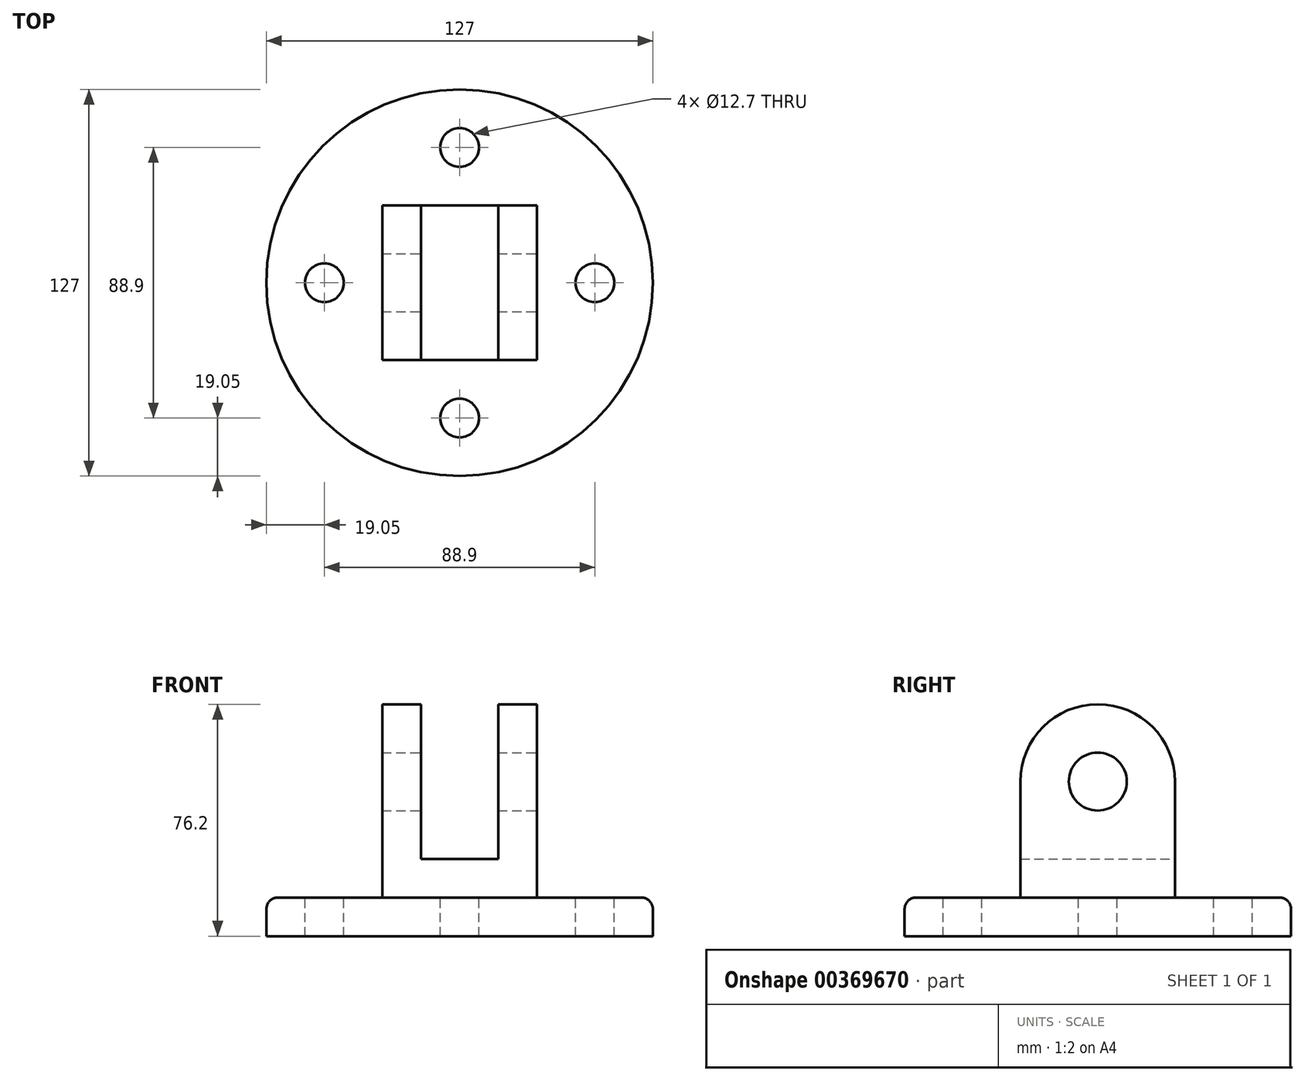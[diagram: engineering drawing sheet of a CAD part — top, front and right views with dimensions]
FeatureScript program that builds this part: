
annotation { "Feature Type Name" : "Feature", "Feature Type Description" : "" }
export const myFeature = defineFeature(function(context is Context, id is Id, definition is map)
    precondition{}
    {
        {
            var Q0;
            Q0=qCreatedBy(makeId("Front.planeOp"),FACE);
            var sketch = newSketch(context, id + "F0", { "sketchPlane" : qUnion([Q0])});
            skLineSegment(sketch, "E0", {"start": v(0, 0) * mm, "end": v(0, 38.1) * mm});
            skLineSegment(sketch, "E1", {"start": v(0, 38.1) * mm, "end": v(12.7, 38.1) * mm});
            skLineSegment(sketch, "E2", {"start": v(12.7, 38.1) * mm, "end": v(12.7, 12.7) * mm});
            skLineSegment(sketch, "E3", {"start": v(12.7, 12.7) * mm, "end": v(38.1, 12.7) * mm});
            skLineSegment(sketch, "E4", {"start": v(38.1, 12.7) * mm, "end": v(38.1, 38.1) * mm});
            skLineSegment(sketch, "E5", {"start": v(38.1, 38.1) * mm, "end": v(50.8, 38.1) * mm});
            skLineSegment(sketch, "E6", {"start": v(50.8, 38.1) * mm, "end": v(50.8, 0) * mm});
            skLineSegment(sketch, "E7", {"start": v(50.8, 0) * mm, "end": v(0, 0) * mm});
            skSolve(sketch);
        }
        {
            var Q0;
            Q0 = qSketchRegion(id + "F0", true);
            extrude(context, id + "F1", {"entities" : qUnion([Q0]), "depth" : 50.8 * mm});
        }
        {
            var Q0;
            Q0=makeQuery(id+"F1.opExtrude","SWEPT_FACE",FACE,{"disambiguationData":[OSD([sQuery(id+"F0.wireOp",EDGE,"E6")])]});
            var sketch = newSketch(context, id + "F2", { "sketchPlane" : qUnion([Q0])});
            skArc(sketch, "E8", {"start": v(0, 38.1) * mm, "mid": v(-25.4, 63.5) * mm, "end": v(-50.8, 38.1) * mm});
            skLineSegment(sketch, "E9", {"start": v(-50.8, 38.1) * mm, "end": v(0, 38.1) * mm});
            skSolve(sketch);
        }
        {
            var Q0;
            Q0 = qSketchRegion(id + "F2", true);
            extrude(context, id + "F3", {"entities" : qUnion([Q0]), "operationType" : NewBodyOperationType.ADD, "oppositeDirection" : true, "depth" : 12.7 * mm});
        }
        {
            var Q0;
            Q0=makeQuery(id+"F1.opExtrude","SWEPT_FACE",FACE,{"disambiguationData":[OSD([sQuery(id+"F0.wireOp",EDGE,"E0")])]});
            var sketch = newSketch(context, id + "F4", { "sketchPlane" : qUnion([Q0])});
            skArc(sketch, "E10", {"start": v(50.8, 38.1) * mm, "mid": v(25.4, 63.5) * mm, "end": v(0, 38.1) * mm});
            skLineSegment(sketch, "E11", {"start": v(50.8, 38.1) * mm, "end": v(0, 38.1) * mm});
            skSolve(sketch);
        }
        {
            var Q0;
            Q0 = qSketchRegion(id + "F4", true);
            extrude(context, id + "F5", {"entities" : qUnion([Q0]), "operationType" : NewBodyOperationType.ADD, "oppositeDirection" : true, "depth" : 12.7 * mm});
        }
        {
            var Q0;
            Q0=makeQuery(id+"F3.boolean.opBoolean","MERGE",FACE,{"derivedFrom":[makeQuery(id+"F1.opExtrude","SWEPT_FACE",FACE,{"disambiguationData":[OSD([sQuery(id+"F0.wireOp",EDGE,"E6")])]}),makeQuery(id+"F3.opExtrude","CAP_FACE",FACE,{"disambiguationData":[OSD([sQuery(id+"F2.wireOp",EDGE,"E8"),sQuery(id+"F2.wireOp",EDGE,"E9")])],"isStart":true})]});
            var sketch = newSketch(context, id + "F6", { "sketchPlane" : qUnion([Q0])});
            skCircle(sketch, "E12", {"center": v(-25.4, 38.1) * mm, "radius": 9.53 * mm});
            skSolve(sketch);
        }
        {
            var Q0;
            Q0 = qSketchRegion(id + "F6", true);
            extrude(context, id + "F7", {"entities" : qUnion([Q0]), "operationType" : NewBodyOperationType.REMOVE, "endBound" : BoundingType.THROUGH_ALL, "oppositeDirection" : true, "depth" : 25.4 * mm});
        }
        {
            var Q0;
            Q0=makeQuery(id+"F1.opExtrude","SWEPT_FACE",FACE,{"disambiguationData":[OSD([sQuery(id+"F0.wireOp",EDGE,"E7")])]});
            var sketch = newSketch(context, id + "F8", { "sketchPlane" : qUnion([Q0])});
            skCircle(sketch, "E13", {"center": v(25.4, 25.4) * mm, "radius": 63.5 * mm});
            skPoint(sketch, "E14", {"position": v(0, 25.4) * mm});
            skPoint(sketch, "E15", {"position": v(25.4, 50.8) * mm});
            skSolve(sketch);
        }
        {
            var Q0;
            Q0 = qSketchRegion(id + "F8", true);
            extrude(context, id + "F9", {"entities" : qUnion([Q0]), "operationType" : NewBodyOperationType.ADD, "depth" : 12.7 * mm});
        }
        {
            var Q0;
            Q0=makeQuery(id+"F9.opExtrude","CAP_FACE",FACE,{"disambiguationData":[OSD([sQuery(id+"F8.wireOp",EDGE,"E13")])],"isStart":true});
            var sketch = newSketch(context, id + "F10", { "sketchPlane" : qUnion([Q0])});
            skCircle(sketch, "E16", {"center": v(25.4, 19.05) * mm, "radius": 6.35 * mm});
            skCircle(sketch, "E17", {"center": v(69.85, -25.4) * mm, "radius": 6.35 * mm});
            skCircle(sketch, "E18", {"center": v(-19.05, -25.4) * mm, "radius": 6.35 * mm});
            skCircle(sketch, "E19", {"center": v(25.4, -69.85) * mm, "radius": 6.35 * mm});
            skPoint(sketch, "E20", {"position": v(25.4, 0) * mm});
            skPoint(sketch, "E21", {"position": v(50.8, -25.4) * mm});
            skPoint(sketch, "E22", {"position": v(0, -25.4) * mm});
            skPoint(sketch, "E23", {"position": v(25.4, -50.8) * mm});
            skCircle(sketch, "E24", {"center": v(25.4, -25.4) * mm, "radius": 44.45 * mm, "construction": true});
            skSolve(sketch);
        }
        {
            var Q0;
            Q0 = qSketchRegion(id + "F10", true);
            extrude(context, id + "F11", {"entities" : qUnion([Q0]), "operationType" : NewBodyOperationType.REMOVE, "endBound" : BoundingType.THROUGH_ALL, "oppositeDirection" : true, "depth" : 25.4 * mm});
        }
        {
            var Q0;
            Q0=makeQuery(id+"F1.opExtrude","SWEPT_EDGE",EDGE,{"disambiguationData":[OSD([sQuery(id+"F0.wireOp",EDGE,"E6"),sQuery(id+"F0.wireOp",EDGE,"E7")])]});
            var Q1;
            Q1=makeQuery(id+"F1.opExtrude","CAP_EDGE",EDGE,{"disambiguationData":[OSD([sQuery(id+"F0.wireOp",EDGE,"E7")])],"isStart":false});
            var Q2;
            Q2=makeQuery(id+"F1.opExtrude","SWEPT_EDGE",EDGE,{"disambiguationData":[OSD([sQuery(id+"F0.wireOp",EDGE,"E0"),sQuery(id+"F0.wireOp",EDGE,"E7")])]});
            var Q3;
            Q3=makeQuery(id+"F1.opExtrude","CAP_EDGE",EDGE,{"disambiguationData":[OSD([sQuery(id+"F0.wireOp",EDGE,"E7")])],"isStart":true});
            var Q4;
            Q4=makeQuery(id+"F9.opExtrude","CAP_EDGE",EDGE,{"disambiguationData":[OSD([sQuery(id+"F8.wireOp",EDGE,"E13")])],"isStart":true});
            fillet(context, id + "F12", {"entities" : qUnion([Q0, Q1, Q2, Q3, Q4]), "radius" : 3.8 * mm, "tangentPropagation" : true, "allowEdgeOverflow" : false});
        }
    });
